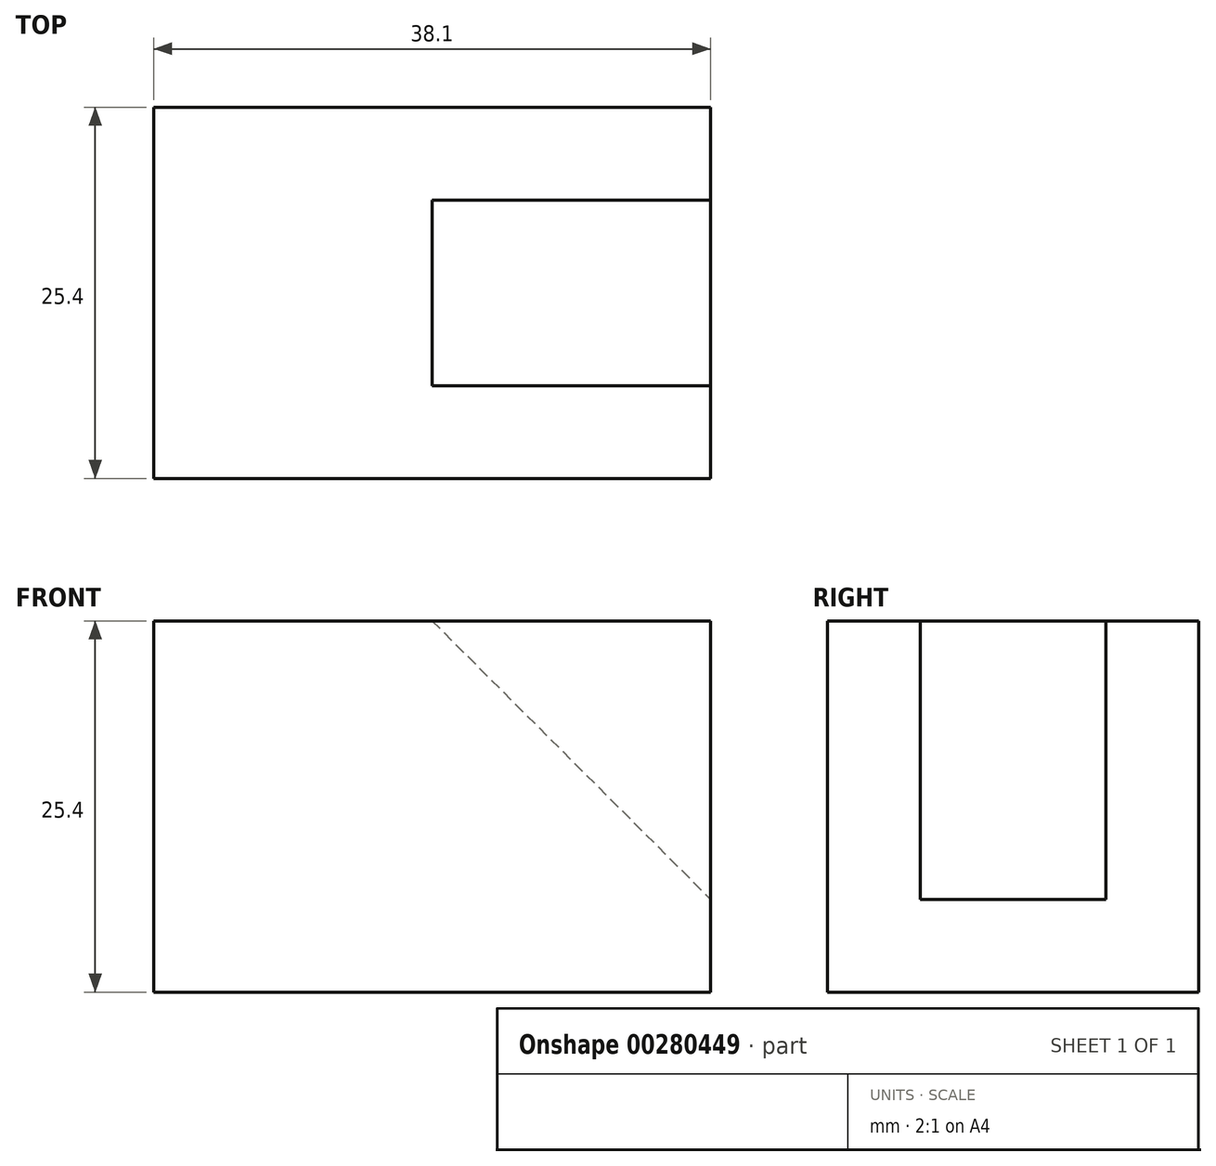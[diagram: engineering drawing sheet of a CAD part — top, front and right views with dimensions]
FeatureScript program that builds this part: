
annotation { "Feature Type Name" : "Feature", "Feature Type Description" : "" }
export const myFeature = defineFeature(function(context is Context, id is Id, definition is map)
    precondition{}
    {
        {
            var Q0;
            Q0=qCreatedBy(makeId("Front.planeOp"),FACE);
            var sketch = newSketch(context, id + "F0", { "sketchPlane" : qUnion([Q0])});
            skLineSegment(sketch, "E0.bottom", {"start": v(0, 0) * mm, "end": v(38.1, 0) * mm});
            skLineSegment(sketch, "E0.top", {"start": v(0, 25.4) * mm, "end": v(38.1, 25.4) * mm});
            skLineSegment(sketch, "E0.left", {"start": v(0, 0) * mm, "end": v(0, 25.4) * mm});
            skLineSegment(sketch, "E0.right", {"start": v(38.1, 0) * mm, "end": v(38.1, 25.4) * mm});
            skSolve(sketch);
        }
        {
            var Q0;
            Q0 = qSketchRegion(id + "F0", true);
            extrude(context, id + "F1", {"entities" : qUnion([Q0]), "depth" : 25.4 * mm});
        }
        {
            var Q0;
            Q0=makeQuery(id+"F1.opExtrude","CAP_FACE",FACE,{"disambiguationData":[OSD([sQuery(id+"F0.wireOp",EDGE,"E0.bottom"),sQuery(id+"F0.wireOp",EDGE,"E0.top"),sQuery(id+"F0.wireOp",EDGE,"E0.left"),sQuery(id+"F0.wireOp",EDGE,"E0.right")])],"isStart":false});
            var sketch = newSketch(context, id + "F2", { "sketchPlane" : qUnion([Q0])});
            skLineSegment(sketch, "E1", {"start": v(38.1, 25.4) * mm, "end": v(19.05, 25.4) * mm});
            skLineSegment(sketch, "E2", {"start": v(19.05, 25.4) * mm, "end": v(38.1, 6.35) * mm});
            skLineSegment(sketch, "E3", {"start": v(38.1, 6.35) * mm, "end": v(38.1, 25.4) * mm});
            skSolve(sketch);
        }
        {
            var Q0;
            Q0 = qSketchRegion(id + "F2", true);
            extrude(context, id + "F3", {"entities" : qUnion([Q0]), "operationType" : NewBodyOperationType.REMOVE, "oppositeDirection" : true, "depth" : 19.05 * mm, "hasSecondDirection" : true, "secondDirectionOppositeDirection" : true, "secondDirectionDepth" : 6.35 * mm});
        }
    });
